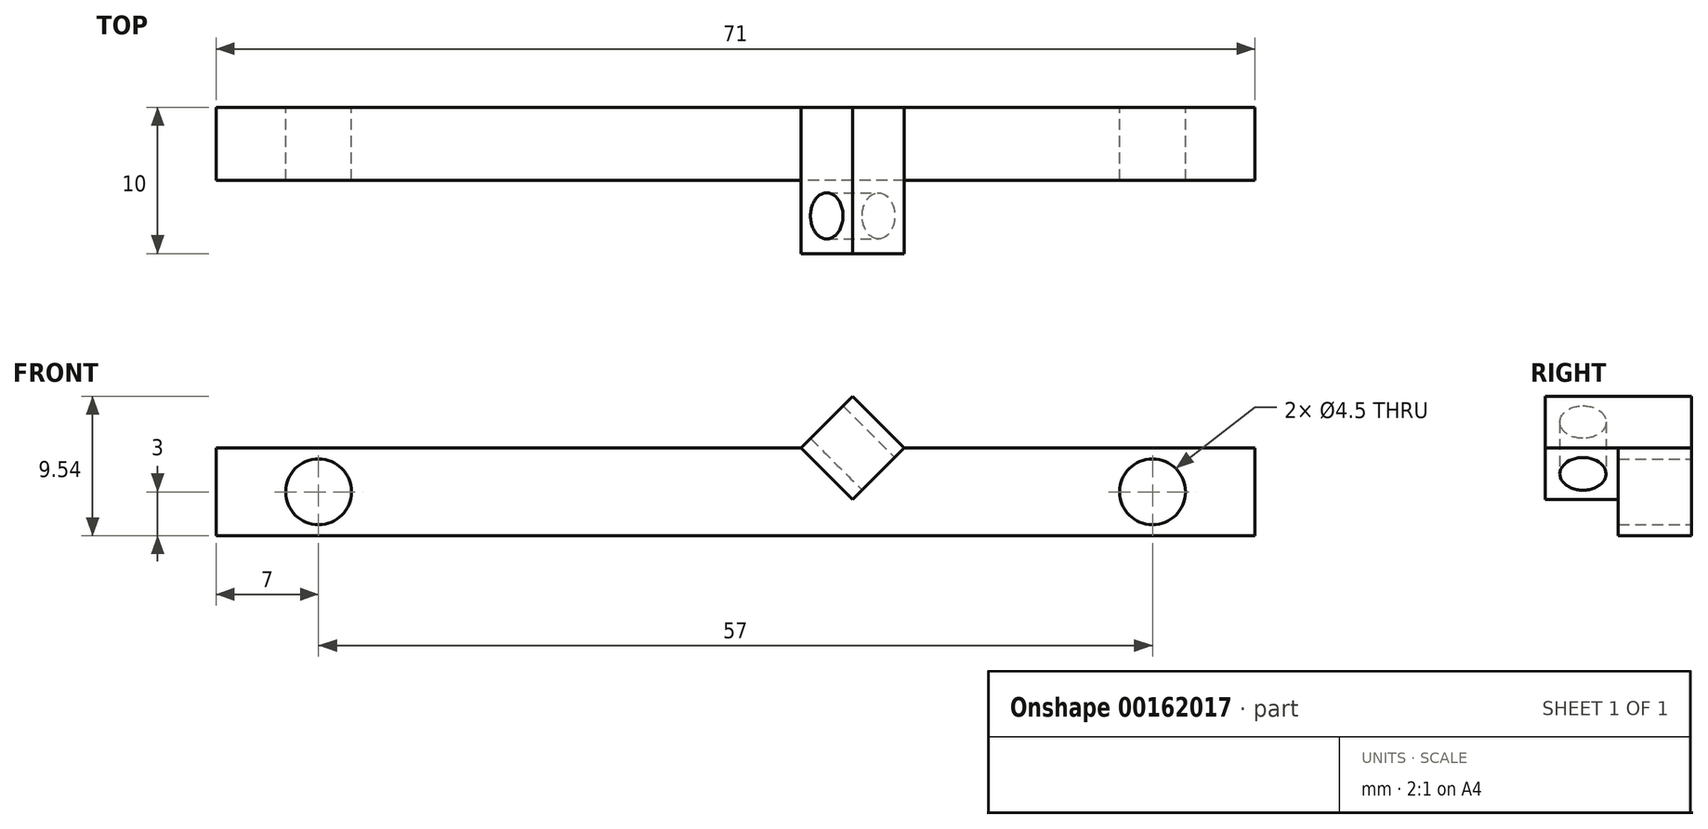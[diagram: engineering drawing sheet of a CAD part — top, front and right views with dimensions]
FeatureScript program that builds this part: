
annotation { "Feature Type Name" : "Feature", "Feature Type Description" : "" }
export const myFeature = defineFeature(function(context is Context, id is Id, definition is map)
    precondition{}
    {
        {
            var Q0;
            Q0=qCreatedBy(makeId("Front.planeOp"),FACE);
            var sketch = newSketch(context, id + "F0", { "sketchPlane" : qUnion([Q0])});
            skLineSegment(sketch, "E0.bottom", {"start": v(35.5, 3) * mm, "end": v(-35.5, 3) * mm});
            skLineSegment(sketch, "E0.top", {"start": v(35.5, -3) * mm, "end": v(-35.5, -3) * mm});
            skLineSegment(sketch, "E0.left", {"start": v(35.5, 3) * mm, "end": v(35.5, -3) * mm});
            skLineSegment(sketch, "E0.right", {"start": v(-35.5, 3) * mm, "end": v(-35.5, -3) * mm});
            skPoint(sketch, "E0.middle", {"position": v(0, 0) * mm});
            skCircle(sketch, "E1", {"center": v(-28.5, 0) * mm, "radius": 2.25 * mm});
            skPoint(sketch, "E1.centerSnap0", {"position": v(-35.5, 0) * mm});
            skLineSegment(sketch, "E2", {"start": v(0, 0) * mm, "end": v(0, 3) * mm, "construction": true});
            skCircle(sketch, "E3.MirrorC", {"center": v(28.5, 0) * mm, "radius": 2.25 * mm});
            skLineSegment(sketch, "E4", {"start": v(16.82, 17.68) * mm, "end": v(19.82, 20.68) * mm});
            skLineSegment(sketch, "E5", {"start": v(4.46, 3) * mm, "end": v(8, 6.54) * mm});
            skLineSegment(sketch, "E6", {"start": v(11.54, 3) * mm, "end": v(8, -0.54) * mm});
            skLineSegment(sketch, "E7", {"start": v(4.46, 3) * mm, "end": v(8, -0.54) * mm});
            skLineSegment(sketch, "E8", {"start": v(8, 6.54) * mm, "end": v(11.54, 3) * mm});
            skSolve(sketch);
        }
        {
            var Q0;
            Q0=qSketchRegion(id+"F0",true);
            extrude(context, id + "F1", {"entities" : qUnion([Q0]), "depth" : 5 * mm});
        }
        {
            var Q0;
            Q0=makeQuery(id+"F1.opExtrude","CAP_FACE",FACE,{"disambiguationData":[OSD([sQuery(id+"F0.wireOp",EDGE,"E0.bottom"),sQuery(id+"F0.wireOp",EDGE,"E0.top"),sQuery(id+"F0.wireOp",EDGE,"E0.left"),sQuery(id+"F0.wireOp",EDGE,"E0.right"),sQuery(id+"F0.wireOp",EDGE,"E1"),sQuery(id+"F0.wireOp",EDGE,"E3.MirrorC"),sQuery(id+"F0.wireOp",EDGE,"E5"),sQuery(id+"F0.wireOp",EDGE,"E8")])],"isStart":false});
            var sketch = newSketch(context, id + "F2", { "sketchPlane" : qUnion([Q0])});
            skLineSegment(sketch, "E9", {"start": v(8, 6.54) * mm, "end": v(4.46, 3) * mm});
            skLineSegment(sketch, "E10", {"start": v(8, 6.54) * mm, "end": v(11.54, 3) * mm});
            skLineSegment(sketch, "E11", {"start": v(11.54, 3) * mm, "end": v(8, -0.54) * mm});
            skLineSegment(sketch, "E12", {"start": v(8, -0.54) * mm, "end": v(4.46, 3) * mm});
            skSolve(sketch);
        }
        {
            var Q0;
            Q0 = qSketchRegion(id + "F2", true);
            extrude(context, id + "F3", {"entities" : qUnion([Q0]), "operationType" : NewBodyOperationType.ADD, "depth" : 5 * mm});
        }
        {
            var Q0;
            Q0=makeQuery(id+"F3.opExtrude","SWEPT_FACE",FACE,{"disambiguationData":[OSD([sQuery(id+"F2.wireOp",EDGE,"E11")])]});
            var sketch = newSketch(context, id + "F4", { "sketchPlane" : qUnion([Q0])});
            skPoint(sketch, "E13.centerSnap0", {"position": v(-10, 7.78) * mm});
            skCircle(sketch, "E14", {"center": v(-7.42, 7.78) * mm, "radius": 1.57 * mm});
            skSolve(sketch);
        }
        {
            var Q0;
            Q0 = qSketchRegion(id + "F4", true);
            extrude(context, id + "F5", {"entities" : qUnion([Q0]), "operationType" : NewBodyOperationType.REMOVE, "endBound" : BoundingType.THROUGH_ALL, "oppositeDirection" : true, "depth" : 25 * mm});
        }
    });
